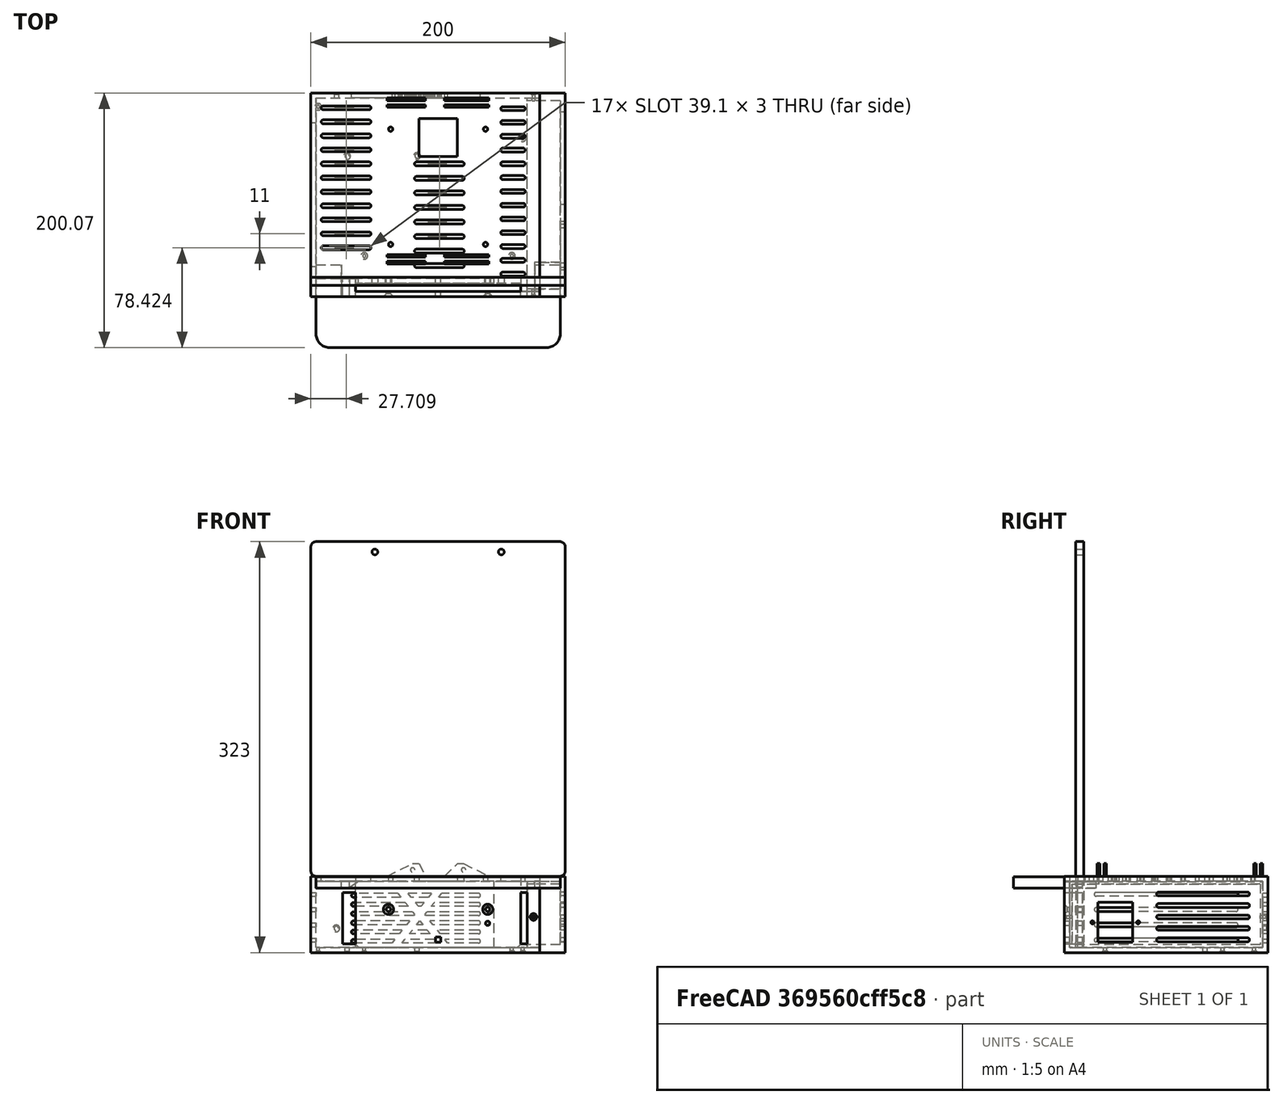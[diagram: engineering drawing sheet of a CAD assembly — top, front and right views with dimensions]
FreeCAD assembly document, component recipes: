
FREECAD ASSEMBLY — COMPONENT RECIPES ("BaseBox")

This assembly document has 5 components, labeled P0..P4 below (a component is one placed body or linked part). 2 of them carry a construction recipe — the FreeCAD feature program that regenerates the part from scratch, quoted from this document or its linked companion documents; the rest are supplied as boundary geometry only. No exploded tour is included for this assembly.
COMPONENT P0 — recipe-attached ("Shank Shield Body", modeled in this document).
Construction recipe (the document's own serialized feature program — sketch geometry with constraints, then the solid features built on it; lengths are millimeters unless a unit is written):

FEATURE [Sketcher::SketchObject] Sketch033  label="Shank Shield Sketch"
  ArcFitTolerance = 1e-06
  AttachmentSupport = -> [XZ_Plane005]
  FullyConstrained = true
  MakeInternals = false
  MapMode = 5
  Placement = pos=(0,0,0) rot=(1,0,0;1.5708rad)
  expr: Constraints[12] = <<Monitor Chassis Parameters>>.GSBasePowerBoxHeight - <<Monitor Chassis Parameters>>.GSBasePowerBoxSideThickness
  expr: Constraints[13] = 0.5 * (<<Monitor Chassis Parameters>>.GSBasePowerBoxWidth - <<Monitor Chassis Parameters>>.GSShankShieldWidth) + 0.5 * <<Monitor Chassis Parameters>>.GSBaseBoxCapOuterWidth
  expr: Constraints[14] = <<Monitor Chassis Parameters>>.GSShankShieldWidth
  expr: Constraints[15] = 0.5 * (<<Monitor Chassis Parameters>>.GSBasePowerBoxWidth - <<Monitor Chassis Parameters>>.GSShankShieldWidth) + 0.5 * <<Monitor Chassis Parameters>>.GSBaseBoxCapOuterWidth
  expr: Constraints[16] = <<Monitor Chassis Parameters>>.GSTowerFourthFloorHeight + 2 * <<Monitor Chassis Parameters>>.GSTowerFloorThickness
  expr: Constraints[22] = <<Monitor Chassis Parameters>>.GSShankShieldCornerFilletRadius
  expr: Constraints[43] = <<Monitor Chassis Parameters>>.GSShankShieldCornerFilletRadius
  expr: Constraints[44] = <<Monitor Chassis Parameters>>.GSShankShieldCornerFilletRadius
  expr: Constraints[45] = <<Monitor Chassis Parameters>>.GSShankShieldCornerFilletRadius
  expr: Constraints[46] = <<Monitor Chassis Parameters>>.GSShankShieldCornerFilletRadius
  expr: Constraints[47] = <<Monitor Chassis Parameters>>.GSShankShieldCornerFilletRadius
  expr: Constraints[48] = <<Monitor Chassis Parameters>>.GSTowerFeetThickness + <<Monitor Chassis Parameters>>.GSTowerFourthFloorHeight - 1.5 * <<Monitor Chassis Parameters>>.GSM4TappingScrewHoleDiameter
  expr: Constraints[49] = <<Monitor Chassis Parameters>>.GSM4TappingScrewHoleDiameter + 1.1
  expr: Constraints[50] = <<Monitor Chassis Parameters>>.GSM4TappingScrewHoleDiameter + 1.1
  expr: Constraints[52] = <<Monitor Chassis Parameters>>.GSBackPlateWidth - 3 * <<Monitor Chassis Parameters>>.GSM4TappingScrewHoleDiameter
  expr: Constraints[53] = 0.5 * (<<Monitor Chassis Parameters>>.GSBasePowerBoxWidth + <<Monitor Chassis Parameters>>.GSBaseBoxCapOuterWidth - <<Monitor Chassis Parameters>>.GSBackPlateWidth) + 1.5 * <<Monitor Chassis Parameters>>.GSM4TappingScrewHoleDiameter
  expr: Constraints[54] = <<Monitor Chassis Parameters>>.GSM4TappingScrewHoleDiameter + 1.1
  expr: Constraints[55] = <<Monitor Chassis Parameters>>.GSM4TappingScrewHoleDiameter + 1.1
  expr: Constraints[57] = <<Monitor Chassis Parameters>>.GSShankShieldBaseBoxSecurementHoleHeight
  expr: Constraints[58] = 0.5 * (<<Monitor Chassis Parameters>>.GSBasePowerBoxWidth + <<Monitor Chassis Parameters>>.GSBaseBoxCapOuterWidth) - 0.3 * <<Monitor Chassis Parameters>>.GSShankShieldWidth
  expr: Constraints[59] = 0.5 * (<<Monitor Chassis Parameters>>.GSBasePowerBoxWidth + <<Monitor Chassis Parameters>>.GSBaseBoxCapOuterWidth) + 0.3 * <<Monitor Chassis Parameters>>.GSShankShieldWidth
  sketch-geometry (24):
    g0: LineSegment StartX=4.24264 StartY=319 StartZ=0 EndX=195.757 EndY=319 EndZ=0
    g1: LineSegment StartX=200 StartY=314.757 StartZ=0 EndX=200 EndY=60.2426 EndZ=0
    g2: LineSegment StartX=195.757 StartY=56 StartZ=0 EndX=165 EndY=56 EndZ=0
    g3: LineSegment StartX=165 StartY=56 StartZ=0 EndX=165 EndY=4.24264 EndZ=0
    g4: LineSegment StartX=160.757 StartY=0 StartZ=0 EndX=39.2426 EndY=0 EndZ=0
    g5: LineSegment StartX=35 StartY=4.24264 StartZ=0 EndX=35 EndY=56 EndZ=0
    g6: LineSegment StartX=35 StartY=56 StartZ=0 EndX=4.24264 EndY=56 EndZ=0
    g7: LineSegment StartX=0 StartY=60.2426 StartZ=0 EndX=0 EndY=314.757 EndZ=0
    g8: ArcOfCircle CenterX=4.24264 CenterY=314.757 CenterZ=0 NormalX=0 NormalY=0 NormalZ=1 AngleXU=0 Radius=4.24264 StartAngle=1.5708 EndAngle=3.14159
    g9: GeomPoint [constr] X=0 Y=319 Z=0
    g10: ArcOfCircle CenterX=195.757 CenterY=314.757 CenterZ=0 NormalX=0 NormalY=0 NormalZ=1 AngleXU=0 Radius=4.24264 StartAngle=2.7e-15 EndAngle=1.5708
    g11: GeomPoint [constr] X=200 Y=319 Z=0
    g12: ArcOfCircle CenterX=4.24264 CenterY=60.2426 CenterZ=0 NormalX=0 NormalY=0 NormalZ=1 AngleXU=0 Radius=4.24264 StartAngle=3.14159 EndAngle=4.71239
    g13: GeomPoint [constr] X=0 Y=56 Z=0
    g14: ArcOfCircle CenterX=195.757 CenterY=60.2426 CenterZ=0 NormalX=0 NormalY=0 NormalZ=1 AngleXU=0 Radius=4.24264 StartAngle=4.71239 EndAngle=6.28319
    g15: GeomPoint [constr] X=200 Y=56 Z=0
    g16: ArcOfCircle CenterX=39.2426 CenterY=4.24264 CenterZ=0 NormalX=0 NormalY=0 NormalZ=1 AngleXU=0 Radius=4.24264 StartAngle=3.14159 EndAngle=4.71239
    g17: GeomPoint [constr] X=35 Y=0 Z=0
    g18: ArcOfCircle CenterX=160.757 CenterY=4.24264 CenterZ=0 NormalX=0 NormalY=0 NormalZ=1 AngleXU=0 Radius=4.24264 StartAngle=4.71239 EndAngle=6.28319
    g19: GeomPoint [constr] X=165 Y=0 Z=0
    g20: Circle CenterX=50.3 CenterY=310.9 CenterZ=0 NormalX=0 NormalY=0 NormalZ=1 AngleXU=0 Radius=2.25
    g21: Circle CenterX=149.7 CenterY=310.9 CenterZ=0 NormalX=0 NormalY=0 NormalZ=1 AngleXU=0 Radius=2.25
    g22: Circle CenterX=61 CenterY=30 CenterZ=0 NormalX=0 NormalY=0 NormalZ=1 AngleXU=0 Radius=2.25
    g23: Circle CenterX=139 CenterY=30 CenterZ=0 NormalX=0 NormalY=0 NormalZ=1 AngleXU=0 Radius=2.25
  constraints (60):
    c: Horizontal(g0)
    c: Vertical(g1)
    c: Horizontal(g2)
    c: Coincident(g3,g2)
    c: PointOnObject(g19,g-1)
    c: Vertical(g3)
    c: Horizontal(g4)
    c: Vertical(g5)
    c: Coincident(g6,g5)
    c: Horizontal(g6)
    c: Vertical(g7)
    c: Horizontal(g5,g2)
    c: DistanceY(g17,g5) = 56
    c: DistanceX(g13,g5) = 35
    c: DistanceX(g5,g2) = 130
    c: DistanceX(g2,g15) = 35
    c: DistanceY(g13,g9) = 263
    c: PointOnObject(g9,g0)
    c: PointOnObject(g9,g7)
    c: Tangent(g0,g8) = 1.5708
    c: Tangent(g7,g8) = 1.5708
    c: Vertical(g13,g-1)
    c: Distance(g9,g8) = 6
    c: PointOnObject(g11,g0)
    c: PointOnObject(g11,g1)
    c: Tangent(g0,g10) = 1.5708
    c: Tangent(g1,g10) = 1.5708
    c: PointOnObject(g13,g6)
    c: PointOnObject(g13,g7)
    c: Tangent(g6,g12) = 1.5708
    c: Tangent(g7,g12) = 1.5708
    c: PointOnObject(g15,g1)
    c: PointOnObject(g15,g2)
    c: Tangent(g1,g14) = 1.5708
    c: Tangent(g2,g14) = 1.5708
    c: PointOnObject(g17,g4)
    c: PointOnObject(g17,g5)
    c: Tangent(g4,g16) = 1.5708
    c: Tangent(g5,g16) = 1.5708
    c: PointOnObject(g19,g3)
    c: PointOnObject(g19,g4)
    c: Tangent(g3,g18) = 1.5708
    c: Tangent(g4,g18) = 1.5708
    c: Distance(g11,g10) = 6
    c: Distance(g13,g12) = 6
    c: Distance(g14,g15) = 6
    c: Distance(g19,g18) = 6
    c: Distance(g16,g17) = 6
    c: DistanceY(g5,g20) = 254.9
    c: Diameter(g20) = 4.5
    c: Diameter(g21) = 4.5
    c: Horizontal(g20,g21)
    c: DistanceX(g20,g21) = 99.4
    c: DistanceX(g-1,g20) = 50.3
    c: Diameter(g22) = 4.5
    c: Diameter(g23) = 4.5
    c: Horizontal(g22,g23)
    c: DistanceY(g-1,g22) = 30
    c: DistanceX(g-1,g22) = 61
    c: DistanceX(g-1,g23) = 139
FEATURE [PartDesign::Pad] Pad009  label="Shank Shield Pad"
  Direction = (0,-1,2e-16)
  Length = 6.35
  Length2 = 10
  Placement = pos=(0,0,0) rot=(1,0,0;1.5708rad)
  Profile = -> Sketch033
  ReferenceAxis = -> Sketch033 [N_Axis]
  Suppressed = false
  Type = 0
  expr: Length = <<Monitor Chassis Parameters>>.GSShankShieldThickness
FEATURE [PartDesign::Body] Body004  label="Shank Shield Body"
  AllowCompound = false
  Group = -> [Sketch033,Pad009]
  Origin = -> Origin005
  Placement = pos=(0,-64.8,0) rot=(0,0,1;0rad)
  Tip = -> Pad009
COMPONENT P1 — geometry summary ("JR-101-1F008"; no construction recipe available for this part):
  bounding box: 44.0 x 33.0 x 27.7 mm
  tessellated surface: 14,122 triangles
  volume: 8508 mm^3 (21% of its bounding box)
COMPONENT P2 — geometry summary ("LRS-154"; no construction recipe available for this part):
  bounding box: 159.0 x 97.0 x 30.0 mm
  tessellated surface: 83,726 triangles
  volume: 73054 mm^3 (16% of its bounding box)
COMPONENT P3 — recipe-attached ("Tower Part", modeled in this document).
Construction recipe (the document's own serialized feature program — sketch geometry with constraints, then the solid features built on it; lengths are millimeters unless a unit is written):

FEATURE [Sketcher::SketchObject] Sketch  label="BaseBox Left Side Sketch"
  ArcFitTolerance = 1e-06
  AttachmentSupport = -> [YZ_Plane001]
  FullyConstrained = true
  MakeInternals = false
  MapMode = 5
  Placement = pos=(0,0,0) rot=(0.57735,0.57735,0.57735;2.0944rad)
  expr: Constraints[10] = <<Monitor Chassis Parameters>>.GSBasePowerBoxHeight - 2 * <<Monitor Chassis Parameters>>.GSBasePowerBoxSideThickness
  expr: Constraints[8] = <<Monitor Chassis Parameters>>.GSBasePowerBoxDepth - 2 * <<Monitor Chassis Parameters>>.GSBasePowerBoxSideThickness
  expr: Constraints[9] = 0.5 * (<<Monitor Chassis Parameters>>.GSBasePowerBoxDepth - 2 * <<Monitor Chassis Parameters>>.GSBasePowerBoxSideThickness)
  sketch-geometry (4):
    g0: LineSegment StartX=-76 StartY=52 StartZ=0 EndX=-76 EndY=0 EndZ=0
    g1: LineSegment StartX=-76 StartY=0 StartZ=0 EndX=76 EndY=0 EndZ=0
    g2: LineSegment StartX=76 StartY=0 StartZ=0 EndX=76 EndY=52 EndZ=0
    g3: LineSegment StartX=76 StartY=52 StartZ=0 EndX=-76 EndY=52 EndZ=0
  constraints (12):
    c: Coincident(g0,g1)
    c: Coincident(g1,g2)
    c: Coincident(g2,g3)
    c: Coincident(g3,g0)
    c: Vertical(g0)
    c: Vertical(g2)
    c: Horizontal(g1)
    c: Horizontal(g3)
    c: DistanceX(g0,g1) = 152
    c: DistanceX(g0,g-1) = 76
    c: DistanceY(g0,g0) = 52
    c: Horizontal(g-1,g0)
FEATURE [PartDesign::Pad] Pad  label="BaseBox Left Side Pad"
  Direction = (1,0,0)
  Length = 4
  Length2 = 10
  Placement = pos=(0,0,0) rot=(1,1,1;2.0944rad)
  Profile = -> Sketch
  ReferenceAxis = -> Sketch [N_Axis]
  Suppressed = false
  Type = 0
  expr: Length = <<Monitor Chassis Parameters>>.GSBasePowerBoxSideThickness
FEATURE [Sketcher::SketchObject] Sketch001  label="BaseBox Enclosure Sketch"
  ArcFitTolerance = 1e-06
  AttachmentSupport = -> [YZ_Plane001]
  FullyConstrained = true
  MakeInternals = false
  MapMode = 5
  Placement = pos=(0,0,0) rot=(0.57735,0.57735,0.57735;2.0944rad)
  expr: Constraints[16] = 0.5 * (<<Monitor Chassis Parameters>>.GSBasePowerBoxDepth - 2 * <<Monitor Chassis Parameters>>.GSBasePowerBoxSideThickness)
  expr: Constraints[17] = <<Monitor Chassis Parameters>>.GSBasePowerBoxDepth - 2 * <<Monitor Chassis Parameters>>.GSBasePowerBoxSideThickness
  expr: Constraints[18] = <<Monitor Chassis Parameters>>.GSBasePowerBoxHeight - 2 * <<Monitor Chassis Parameters>>.GSBasePowerBoxSideThickness
  expr: Constraints[19] = <<Monitor Chassis Parameters>>.GSBasePowerBoxSideThickness
  expr: Constraints[20] = <<Monitor Chassis Parameters>>.GSBasePowerBoxSideThickness
  expr: Constraints[21] = <<Monitor Chassis Parameters>>.GSBasePowerBoxSideThickness
  expr: Constraints[23] = <<Monitor Chassis Parameters>>.GSBasePowerBoxSideThickness
  sketch-geometry (8):
    g0: LineSegment StartX=-80 StartY=56 StartZ=0 EndX=-80 EndY=-4 EndZ=0
    g1: LineSegment StartX=-80 StartY=-4 StartZ=0 EndX=80 EndY=-4 EndZ=0
    g2: LineSegment StartX=80 StartY=-4 StartZ=0 EndX=80 EndY=56 EndZ=0
    g3: LineSegment StartX=80 StartY=56 StartZ=0 EndX=-80 EndY=56 EndZ=0
    g4: LineSegment StartX=-76 StartY=52 StartZ=0 EndX=-76 EndY=0 EndZ=0
    g5: LineSegment StartX=-76 StartY=0 StartZ=0 EndX=76 EndY=0 EndZ=0
    g6: LineSegment StartX=76 StartY=0 StartZ=0 EndX=76 EndY=52 EndZ=0
    g7: LineSegment StartX=76 StartY=52 StartZ=0 EndX=-76 EndY=52 EndZ=0
  constraints (24):
    c: Coincident(g0,g1)
    c: Coincident(g1,g2)
    c: Coincident(g2,g3)
    c: Coincident(g3,g0)
    c: Vertical(g0)
    c: Vertical(g2)
    c: Horizontal(g1)
    c: Horizontal(g3)
    c: Coincident(g4,g5)
    c: Coincident(g5,g6)
    c: Coincident(g6,g7)
    c: Coincident(g7,g4)
    c: Vertical(g4)
    c: Vertical(g6)
    c: Horizontal(g5)
    c: Horizontal(g7)
    c: DistanceX(g4,g-1) = 76
    c: DistanceX(g4,g5) = 152
    c: DistanceY(g4,g4) = 52
    c: DistanceX(g0,g4) = 4
    c: DistanceY(g4,g0) = 4
    c: DistanceX(g5,g1) = 4
    c: Horizontal(g4,g-1)
    c: DistanceY(g0,g4) = 4
FEATURE [PartDesign::Pad] Pad001  label="BaseBox Enclosure Pad"
  BaseFeature = -> Pad
  Direction = (1,0,0)
  Length = 180
  Length2 = 10
  Placement = pos=(0,0,0) rot=(1,1,1;2.0944rad)
  Profile = -> Sketch001
  ReferenceAxis = -> Sketch001 [N_Axis]
  Suppressed = false
  Type = 0
  expr: Length = <<Monitor Chassis Parameters>>.GSBasePowerBoxWidth
FEATURE [PartDesign::Plane] DatumPlane  label="BaseBox Side Datum Plane"
  AttachmentOffset = pos=(0,0,-80) rot=(0,0,1;0rad)
  AttachmentSupport = -> [XZ_Plane001]
  Length = 249.363
  MapMode = 5
  Placement = pos=(0,80,-1.78e-14) rot=(1,0,0;1.5708rad)
  ResizeMode = 0
  Width = 119.363
  expr: .AttachmentOffset.Base.z = -0.5 * <<Monitor Chassis Parameters>>.GSBasePowerBoxDepth
FEATURE [Sketcher::SketchObject] Sketch002  label="BaseBox Side Screw Holes Sketch"
  ArcFitTolerance = 1e-06
  AttachmentSupport = -> [DatumPlane]
  FullyConstrained = true
  MakeInternals = false
  MapMode = 5
  Placement = pos=(0,80,-1.78e-14) rot=(1,0,0;1.5708rad)
  expr: Constraints[0] = <<Monitor Chassis Parameters>>.GSBasePowerBoxSupplyMountingScrewSize
  expr: Constraints[1] = <<Monitor Chassis Parameters>>.GSBasePowerBoxSupplyMountingScrewSize
  expr: Constraints[2] = <<Monitor Chassis Parameters>>.GSBasePowerBoxSupplyMountingLeftScrewOffsetFromRight
  expr: Constraints[3] = <<Monitor Chassis Parameters>>.GSBasePowerBoxSupplyMountingScrewOffsetFromRight
  expr: Constraints[4] = <<Monitor Chassis Parameters>>.GSBasePowerBoxSupplyMountingRightScrewHeight1
  expr: Constraints[5] = <<Monitor Chassis Parameters>>.GSBasePowerBoxSupplyMountingLeftScrewHeight
  sketch-geometry (2):
    g0: Circle CenterX=94 CenterY=15 CenterZ=0 NormalX=0 NormalY=0 NormalZ=1 AngleXU=0 Radius=1.7
    g1: Circle CenterX=20 CenterY=15 CenterZ=0 NormalX=0 NormalY=0 NormalZ=1 AngleXU=0 Radius=1.7
  constraints (6):
    c: Diameter(g0) = 3.4
    c: Diameter(g1) = 3.4
    c: DistanceX(g-1,g0) = 94
    c: DistanceX(g-1,g1) = 20
    c: DistanceY(g-1,g1) = 15
    c: DistanceY(g-1,g0) = 15
FEATURE [PartDesign::Hole] Hole  label="BaseBox Side Screw Holes"
  BaseFeature = -> Pad001
  CustomThreadClearance = 0
  Depth = 25
  DepthType = 0
  Diameter = 3.4
  DrillForDepth = false
  DrillPoint = 1
  DrillPointAngle = 118
  HoleCutCountersinkAngle = 90
  HoleCutCustomValues = false
  HoleCutDepth = 0
  HoleCutDiameter = 5.3
  HoleCutType = 2
  ModelThread = false
  Placement = pos=(0,0,0) rot=(1,1,1;2.0944rad)
  Profile = -> Sketch002
  Reversed = true
  Suppressed = false
  Tapered = false
  TaperedAngle = 90
  ThreadClass = 0
  ThreadDepth = 25
  ThreadDepthType = 0
  ThreadDirection = 0
  ThreadFit = 0
  ThreadSize = 0
  ThreadType = 0
  Threaded = false
  UseCustomThreadClearance = false
  expr: Diameter = <<Monitor Chassis Parameters>>.GSBasePowerBoxSupplyMountingScrewSize
  expr: HoleCutDiameter = <<Monitor Chassis Parameters>>.GSM3BoltCountersinkDiameter
FEATURE [PartDesign::Plane] DatumPlane001  label="BaseBox Bottom Datum Plane"
  AttachmentOffset = pos=(0,0,-4) rot=(0,0,1;0rad)
  AttachmentSupport = -> [XY_Plane001]
  Length = 258.609
  MapMode = 5
  Placement = pos=(0,0,-4) rot=(0,0,1;0rad)
  ResizeMode = 0
  Width = 197.609
  expr: .AttachmentOffset.Base.z = -<<Monitor Chassis Parameters>>.GSBasePowerBoxSideThickness
FEATURE [Sketcher::SketchObject] Sketch003  label="BaseBox Bottom Screw Holes Sketch"
  ArcFitTolerance = 1e-06
  AttachmentSupport = -> [DatumPlane001]
  FullyConstrained = true
  MakeInternals = false
  MapMode = 5
  Placement = pos=(0,0,-4) rot=(0,0,1;0rad)
  expr: Constraints[1] = <<Monitor Chassis Parameters>>.GSBasePowerBoxSupplyMountingScrewSize
  expr: Constraints[2] = <<Monitor Chassis Parameters>>.GSBasePowerBoxSupplyMountingScrewSize
  expr: Constraints[3] = <<Monitor Chassis Parameters>>.GSBasePowerBoxSupplyMountingBottomScrewsBackOffset
  expr: Constraints[4] = <<Monitor Chassis Parameters>>.GSBasePowerBoxSupplyMountingBottomScrewOffsetFromLeft1
  expr: Constraints[5] = <<Monitor Chassis Parameters>>.GSBasePowerBoxSupplyMountingBottomScrewOffsetFromLeft2
  sketch-geometry (2):
    g0: Circle CenterX=83.5 CenterY=30.5 CenterZ=0 NormalX=0 NormalY=0 NormalZ=1 AngleXU=0 Radius=1.7
    g1: Circle CenterX=28.5 CenterY=30.5 CenterZ=0 NormalX=0 NormalY=0 NormalZ=1 AngleXU=0 Radius=1.7
  constraints (6):
    c: Horizontal(g0,g1)
    c: Diameter(g0) = 3.4
    c: Diameter(g1) = 3.4
    c: DistanceY(g1) = 30.5
    c: DistanceX(g-1,g0) = 83.5
    c: DistanceX(g-1,g1) = 28.5
FEATURE [PartDesign::Hole] Hole001  label="BaseBox Bottom Screw Holes"
  BaseFeature = -> Hole
  CustomThreadClearance = 0
  Depth = 25
  DepthType = 0
  Diameter = 3.4
  DrillForDepth = false
  DrillPoint = 1
  DrillPointAngle = 118
  HoleCutCountersinkAngle = 90
  HoleCutCustomValues = false
  HoleCutDepth = 0
  HoleCutDiameter = 5.3
  HoleCutType = 2
  ModelThread = false
  Placement = pos=(0,0,0) rot=(1,1,1;2.0944rad)
  Profile = -> Sketch003
  Reversed = true
  Suppressed = false
  Tapered = false
  TaperedAngle = 90
  ThreadClass = 0
  ThreadDepth = 25
  ThreadDepthType = 0
  ThreadDirection = 0
  ThreadFit = 0
  ThreadSize = 0
  ThreadType = 0
  Threaded = false
  UseCustomThreadClearance = false
  expr: Diameter = <<Monitor Chassis Parameters>>.GSBasePowerBoxSupplyMountingScrewSize
  expr: HoleCutDiameter = <<Monitor Chassis Parameters>>.GSM3BoltCountersinkDiameter
FEATURE [Sketcher::SketchObject] Sketch005  label="BaseBox Left Side Slots Sketch"
  ArcFitTolerance = 1e-06
  AttachmentSupport = -> [YZ_Plane001]
  FullyConstrained = false
  MakeInternals = false
  MapMode = 5
  Placement = pos=(0,0,0) rot=(0.57735,0.57735,0.57735;2.0944rad)
  expr: Constraints[3] = <<Monitor Chassis Parameters>>.GSBasePowerBoxCoolingSlotWidth
  sketch-geometry (4):
    g0: LineSegment StartX=55 StartY=4.30289 StartZ=0 EndX=-55 EndY=4.30289 EndZ=0
    g1: LineSegment StartX=55 StartY=7.30289 StartZ=0 EndX=-55 EndY=7.30289 EndZ=0
    g2: ArcOfCircle CenterX=55 CenterY=5.80289 CenterZ=0 NormalX=0 NormalY=0 NormalZ=1 AngleXU=0 Radius=1.5 StartAngle=4.71239 EndAngle=7.85398
    g3: ArcOfCircle CenterX=-55 CenterY=5.80289 CenterZ=0 NormalX=0 NormalY=0 NormalZ=1 AngleXU=0 Radius=1.5 StartAngle=1.5708 EndAngle=4.71239
  constraints (13):
    c: Horizontal(g0)
    c: Horizontal(g1)
    c: Vertical(g0,g1)
    c: DistanceY(g0,g1) = 3
    c: DistanceX(g-1,g0) = 55
    c: DistanceX(g0,g-1) = 55
    c: Coincident(g2,g1)
    c: Coincident(g2,g0)
    c: Vertical(g2,g1)
    c: Vertical(g0,g1)
    c: Coincident(g3,g1)
    c: Coincident(g3,g0)
    c: Vertical(g0,g3)
FEATURE [PartDesign::Pocket] Pocket  label="BaseBox Left Side Slots Pocket"
  BaseFeature = -> Hole001
  Direction = (-1,0,0)
  Length = 0
  Length2 = 5
  Placement = pos=(0,0,0) rot=(1,1,1;2.0944rad)
  Profile = -> Sketch005
  ReferenceAxis = -> Sketch005 [N_Axis]
  Reversed = true
  Suppressed = false
  Type = 2
FEATURE [PartDesign::LinearPattern] LinearPattern
  BaseFeature = -> Pocket
  Direction = -> Z_Axis001
  Length = 36
  Mode = 1
  Occurrences = 4
  Offset = 12
  Originals = -> [Pocket]
  Placement = pos=(0,0,0) rot=(1,1,1;2.0944rad)
  Suppressed = false
  TransformMode = 0
  expr: Offset = 0.2 * <<Monitor Chassis Parameters>>.GSBasePowerBoxHeight
FEATURE [PartDesign::Plane] DatumPlane002  label="BaseBox Top DatumPlane"
  AttachmentOffset = pos=(0,0,56) rot=(0,0,1;0rad)
  AttachmentSupport = -> [XY_Plane001]
  Length = 258.609
  MapMode = 5
  Placement = pos=(0,0,56) rot=(0,0,1;0rad)
  ResizeMode = 0
  Width = 197.609
  expr: .AttachmentOffset.Base.z = <<Monitor Chassis Parameters>>.GSBasePowerBoxHeight - <<Monitor Chassis Parameters>>.GSBasePowerBoxSideThickness
FEATURE [Sketcher::SketchObject] Sketch006  label="BaseBox Top Holes Sketch"
  ArcFitTolerance = 1e-06
  AttachmentSupport = -> [DatumPlane002]
  FullyConstrained = true
  MakeInternals = false
  MapMode = 5
  Placement = pos=(0,0,56) rot=(0,0,1;0rad)
  expr: Constraints[10] = 0.5 * (<<Monitor Chassis Parameters>>.GSBasePowerBoxWidth - <<Monitor Chassis Parameters>>.GSShankShieldWidth) + 0.5 * <<Monitor Chassis Parameters>>.GSBaseBoxCapOuterWidth
  expr: Constraints[11] = 0.5 * <<Monitor Chassis Parameters>>.GSBasePowerBoxDepth - <<Monitor Chassis Parameters>>.GSBasePowerBoxSideThickness
  expr: Constraints[8] = <<Monitor Chassis Parameters>>.GSShankShieldThickness
  expr: Constraints[9] = <<Monitor Chassis Parameters>>.GSShankShieldWidth
  sketch-geometry (4):
    g0: LineSegment StartX=35 StartY=-69.65 StartZ=0 EndX=35 EndY=-76 EndZ=0
    g1: LineSegment StartX=35 StartY=-76 StartZ=0 EndX=165 EndY=-76 EndZ=0
    g2: LineSegment StartX=165 StartY=-76 StartZ=0 EndX=165 EndY=-69.65 EndZ=0
    g3: LineSegment StartX=165 StartY=-69.65 StartZ=0 EndX=35 EndY=-69.65 EndZ=0
  constraints (12):
    c: Coincident(g0,g1)
    c: Coincident(g1,g2)
    c: Coincident(g2,g3)
    c: Coincident(g3,g0)
    c: Vertical(g0)
    c: Vertical(g2)
    c: Horizontal(g1)
    c: Horizontal(g3)
    c: DistanceY(g0,g0) = 6.35
    c: DistanceX(g0,g2) = 130
    c: DistanceX(g-1,g0) = 35
    c: DistanceY(g0,g-1) = 76
FEATURE [PartDesign::Pocket] Pocket001  label="Shank Shield Pocket"
  BaseFeature = -> LinearPattern
  Direction = (0,0,-1)
  Length = 5
  Length2 = 5
  Placement = pos=(0,0,0) rot=(1,1,1;2.0944rad)
  Profile = -> Sketch006
  ReferenceAxis = -> Sketch006 [N_Axis]
  Suppressed = false
  Type = 2
FEATURE [Sketcher::SketchObject] Sketch007  label="Shank Shield Position Ribs Sketch"
  ArcFitTolerance = 1e-06
  AttachmentSupport = -> [XY_Plane001]
  FullyConstrained = true
  MakeInternals = false
  MapMode = 5
  expr: Constraints[12] = <<Monitor Chassis Parameters>>.GSBasePowerBoxSideThickness
  expr: Constraints[13] = <<Monitor Chassis Parameters>>.GSBasePowerBoxSideThickness
  expr: Constraints[14] = <<Monitor Chassis Parameters>>.GSShankShieldThickness
  expr: Constraints[15] = 0.5 * <<Monitor Chassis Parameters>>.GSBasePowerBoxDepth - <<Monitor Chassis Parameters>>.GSBasePowerBoxSideThickness
  expr: Constraints[17] = 0.5 * (<<Monitor Chassis Parameters>>.GSBasePowerBoxWidth - <<Monitor Chassis Parameters>>.GSShankShieldWidth) + 0.5 * <<Monitor Chassis Parameters>>.GSBaseBoxCapOuterWidth - <<Monitor Chassis Parameters>>.GSBasePowerBoxSideThickness
  sketch-geometry (6):
    g0: LineSegment StartX=4 StartY=-76 StartZ=0 EndX=35 EndY=-76 EndZ=0
    g1: LineSegment StartX=35 StartY=-76 StartZ=0 EndX=35 EndY=-69.65 EndZ=0
    g2: LineSegment StartX=35 StartY=-69.65 StartZ=0 EndX=144 EndY=-69.65 EndZ=0
    g3: LineSegment StartX=144 StartY=-69.65 StartZ=0 EndX=144 EndY=-65.65 EndZ=0
    g4: LineSegment StartX=144 StartY=-65.65 StartZ=0 EndX=4 EndY=-65.65 EndZ=0
    g5: LineSegment StartX=4 StartY=-65.65 StartZ=0 EndX=4 EndY=-76 EndZ=0
  constraints (18):
    c: Horizontal(g0)
    c: Coincident(g1,g0)
    c: Vertical(g1)
    c: Coincident(g2,g1)
    c: Horizontal(g2)
    c: Coincident(g3,g2)
    c: Vertical(g3)
    c: Coincident(g4,g3)
    c: Horizontal(g4)
    c: Coincident(g5,g4)
    c: Coincident(g5,g0)
    c: Vertical(g5)
    c: DistanceX(g-1,g4) = 4
    c: DistanceY(g2,g3) = 4
    c: DistanceY(g0,g1) = 6.35
    c: DistanceY(g0,g-1) = 76
    c: DistanceX(g4,g3) = 140
    c: DistanceX(g0,g0) = 31
FEATURE [PartDesign::Pad] Pad002  label="Shank Shield Position Ribs Pad"
  BaseFeature = -> Pocket001
  Direction = (0,0,1)
  Length = 52
  Length2 = 10
  Placement = pos=(0,0,0) rot=(1,1,1;2.0944rad)
  Profile = -> Sketch007
  ReferenceAxis = -> Sketch007 [N_Axis]
  Suppressed = false
  Type = 0
  expr: Length = <<Monitor Chassis Parameters>>.GSBasePowerBoxHeight - 2 * <<Monitor Chassis Parameters>>.GSBasePowerBoxSideThickness
FEATURE [Sketcher::SketchObject] Sketch008  label="Light Shield Sketch"
  ArcFitTolerance = 1e-06
  AttachmentSupport = -> [XY_Plane002]
  FullyConstrained = false
  MakeInternals = false
  MapMode = 5
  expr: Constraints[18] = <<Monitor Chassis Parameters>>.GSLightShieldTabWidth
  expr: Constraints[19] = <<Monitor Chassis Parameters>>.GSLightShieldTabWidth
  expr: Constraints[20] = <<Monitor Chassis Parameters>>.GSLightShieldTabDepth
  expr: Constraints[22] = <<Monitor Chassis Parameters>>.GSLightShieldDepth
  expr: Constraints[28] = <<Monitor Chassis Parameters>>.GSBasePowerBoxWidth + <<Monitor Chassis Parameters>>.GSBaseBoxCapOuterWidth - <<Monitor Chassis Parameters>>.GSBasePowerBoxSideThickness
  expr: Constraints[29] = <<Monitor Chassis Parameters>>.GSBasePowerBoxSideThickness
  sketch-geometry (10):
    g0: LineSegment StartX=4 StartY=-112.141 StartZ=0 EndX=4 EndY=-57.7713 EndZ=0
    g1: LineSegment StartX=4 StartY=-57.7713 StartZ=0 EndX=24 EndY=-57.7713 EndZ=0
    g2: LineSegment StartX=24 StartY=-57.7713 StartZ=0 EndX=24 EndY=-82.7713 EndZ=0
    g3: LineSegment StartX=24 StartY=-82.7713 StartZ=0 EndX=176 EndY=-82.7713 EndZ=0
    g4: LineSegment StartX=176 StartY=-82.7713 StartZ=0 EndX=176 EndY=-57.7713 EndZ=0
    g5: LineSegment StartX=176 StartY=-57.7713 StartZ=0 EndX=196 EndY=-57.7713 EndZ=0
    g6: LineSegment StartX=196 StartY=-57.7713 StartZ=0 EndX=196 EndY=-112.141 EndZ=0
    g7: LineSegment StartX=14.6305 StartY=-122.771 StartZ=0 EndX=185.37 EndY=-122.771 EndZ=0
    g8: ArcOfCircle CenterX=14.6305 CenterY=-112.141 CenterZ=0 NormalX=0 NormalY=0 NormalZ=1 AngleXU=0 Radius=10.6305 StartAngle=3.14159 EndAngle=4.71239
    g9: ArcOfCircle CenterX=185.37 CenterY=-112.141 CenterZ=0 NormalX=0 NormalY=0 NormalZ=1 AngleXU=0 Radius=10.6305 StartAngle=4.71239 EndAngle=6.28319
  constraints (30):
    c: Vertical(g0)
    c: Coincident(g1,g0)
    c: Horizontal(g1)
    c: Coincident(g2,g1)
    c: Vertical(g2)
    c: Coincident(g3,g2)
    c: Horizontal(g3)
    c: Coincident(g4,g3)
    c: Vertical(g4)
    c: Coincident(g5,g4)
    c: Horizontal(g5)
    c: Coincident(g6,g5)
    c: Vertical(g6)
    c: Horizontal(g7)
    c: Coincident(g8,g0)
    c: Coincident(g8,g7)
    c: Coincident(g9,g7)
    c: Coincident(g9,g6)
    c: DistanceX(g0,g1) = 20
    c: DistanceX(g4,g5) = 20
    c: DistanceY(g2,g1) = 25
    c: Horizontal(g1,g4)
    c: DistanceY(g7,g2) = 40
    c: Horizontal(g8,g0)
    c: Horizontal(g9,g6)
    c: Vertical(g8,g7)
    c: Vertical(g9,g7)
    c: Horizontal(g0,g6)
    c: DistanceX(g-1,g5) = 196
    c: DistanceX(g-1,g0) = 4
FEATURE [PartDesign::Pad] Pad003  label="Light Shield Pad"
  Direction = (0,0,1)
  Length = 9
  Length2 = 10
  Profile = -> Sketch008
  ReferenceAxis = -> Sketch008 [N_Axis]
  Suppressed = false
  Type = 0
  expr: Length = <<Monitor Chassis Parameters>>.GSLightShieldThickness + <<Monitor Chassis Parameters>>.GSBasePowerBoxSideThickness
FEATURE [PartDesign::Plane] DatumPlane003  label="BaseBox Front DatumPlane"
  AttachmentOffset = pos=(0,0,80) rot=(0,0,1;0rad)
  AttachmentSupport = -> [XZ_Plane001]
  Length = 249.363
  MapMode = 5
  Placement = pos=(0,-80,1.78e-14) rot=(1,0,0;1.5708rad)
  ResizeMode = 0
  Width = 119.363
  expr: .AttachmentOffset.Base.z = 0.5 * <<Monitor Chassis Parameters>>.GSBasePowerBoxDepth
FEATURE [Sketcher::SketchObject] Sketch009  label="Light Shield Tabs Sketch"
  ArcFitTolerance = 1e-06
  AttachmentSupport = -> [DatumPlane003]
  FullyConstrained = true
  MakeInternals = false
  MapMode = 5
  Placement = pos=(0,-80,1.78e-14) rot=(1,0,0;1.5708rad)
  expr: Constraints[10] = <<Monitor Chassis Parameters>>.GSBasePowerBoxSideThickness
  expr: Constraints[11] = <<Monitor Chassis Parameters>>.GSLightShieldHeight
  expr: Constraints[21] = <<Monitor Chassis Parameters>>.GSLightShieldTabThickness
  expr: Constraints[22] = <<Monitor Chassis Parameters>>.GSLightShieldTabWidth + <<Monitor Chassis Parameters>>.GSPartFitExtraToleranceDistance
  expr: Constraints[23] = <<Monitor Chassis Parameters>>.GSBasePowerBoxWidth + <<Monitor Chassis Parameters>>.GSBaseBoxCapOuterWidth - <<Monitor Chassis Parameters>>.GSBasePowerBoxSideThickness
  expr: Constraints[8] = <<Monitor Chassis Parameters>>.GSLightShieldTabWidth + 6 + <<Monitor Chassis Parameters>>.GSPartFitExtraToleranceDistance
  expr: Constraints[9] = <<Monitor Chassis Parameters>>.GSLightShieldTabThickness + 0.5 * <<Monitor Chassis Parameters>>.GSPartFitExtraToleranceDistance
  sketch-geometry (8):
    g0: LineSegment StartX=4 StartY=46.9 StartZ=0 EndX=30.2 EndY=46.9 EndZ=0
    g1: LineSegment StartX=30.2 StartY=46.9 StartZ=0 EndX=30.2 EndY=52 EndZ=0
    g2: LineSegment StartX=30.2 StartY=52 StartZ=0 EndX=4 EndY=52 EndZ=0
    g3: LineSegment StartX=4 StartY=52 StartZ=0 EndX=4 EndY=46.9 EndZ=0
    g4: LineSegment StartX=175.8 StartY=47 StartZ=0 EndX=196 EndY=47 EndZ=0
    g5: LineSegment StartX=196 StartY=47 StartZ=0 EndX=196 EndY=52 EndZ=0
    g6: LineSegment StartX=196 StartY=52 StartZ=0 EndX=175.8 EndY=52 EndZ=0
    g7: LineSegment StartX=175.8 StartY=52 StartZ=0 EndX=175.8 EndY=47 EndZ=0
  constraints (24):
    c: Coincident(g0,g1)
    c: Coincident(g1,g2)
    c: Coincident(g2,g3)
    c: Coincident(g3,g0)
    c: Horizontal(g0)
    c: Horizontal(g2)
    c: Vertical(g1)
    c: Vertical(g3)
    c: DistanceX(g2,g1) = 26.2
    c: DistanceY(g0,g2) = 5.1
    c: DistanceX(g-1,g0) = 4
    c: DistanceY(g-1,g2) = 52
    c: Coincident(g4,g5)
    c: Coincident(g5,g6)
    c: Coincident(g6,g7)
    c: Coincident(g7,g4)
    c: Horizontal(g4)
    c: Horizontal(g6)
    c: Vertical(g5)
    c: Vertical(g7)
    c: Horizontal(g6,g1)
    c: DistanceY(g4,g5) = 5
    c: DistanceX(g6,g5) = 20.2
    c: DistanceX(g-1,g5) = 196
FEATURE [PartDesign::Pocket] Pocket002  label="Light Shield Tabs Pocket"
  BaseFeature = -> Pad002
  Direction = (0,1,-2e-16)
  Length = 25
  Length2 = 5
  Placement = pos=(0,0,0) rot=(1,1,1;2.0944rad)
  Profile = -> Sketch009
  ReferenceAxis = -> Sketch009 [N_Axis]
  Suppressed = false
  Type = 0
  expr: Length = <<Monitor Chassis Parameters>>.GSLightShieldTabDepth
FEATURE [Sketcher::SketchObject] Sketch010  label="Overhang Fix Sketch 1"
  ArcFitTolerance = 1e-06
  AttachmentSupport = -> [Pad002]
  FullyConstrained = false
  MakeInternals = false
  MapMode = 5
  Placement = pos=(-1.46e-14,-65.65,7.3e-15) rot=(0.57735,0.57735,0.57735;4.18879rad)
  expr: Constraints[6] = <<Monitor Chassis Parameters>>.GSBasePowerBoxHeight - 2 * <<Monitor Chassis Parameters>>.GSBasePowerBoxSideThickness
  sketch-geometry (3):
    g0: LineSegment StartX=47 StartY=29.984 StartZ=0 EndX=52 EndY=36.9429 EndZ=0
    g1: LineSegment StartX=52 StartY=36.9429 StartZ=0 EndX=52 EndY=29.984 EndZ=0
    g2: LineSegment StartX=52 StartY=29.984 StartZ=0 EndX=47 EndY=29.984 EndZ=0
  constraints (7):
    c: Coincident(g1,g0)
    c: Vertical(g1)
    c: Coincident(g2,g1)
    c: Coincident(g2,g0)
    c: Horizontal(g2)
    c: DistanceX(g0,g1) = 5
    c: DistanceX(g-1,g1) = 52
FEATURE [PartDesign::Pocket] Pocket003  label="Overhang Fix Pocket 1"
  BaseFeature = -> Pocket002
  Direction = (0,-1,0)
  Length = 5
  Length2 = 5
  Placement = pos=(0,0,0) rot=(1,1,1;2.0944rad)
  Profile = -> Sketch010
  ReferenceAxis = -> Sketch010 [N_Axis]
  Suppressed = false
  Type = 0
FEATURE [Sketcher::SketchObject] Sketch011  label="BaseBox Cap Side Sketch"
  ArcFitTolerance = 1e-06
  AttachmentSupport = -> [YZ_Plane003]
  FullyConstrained = true
  MakeInternals = false
  MapMode = 5
  Placement = pos=(0,0,0) rot=(0.57735,0.57735,0.57735;2.0944rad)
  expr: Constraints[10] = <<Monitor Chassis Parameters>>.GSBasePowerBoxHeight
  expr: Constraints[12] = <<Monitor Chassis Parameters>>.GSM3TappingScrewHoleDiameter
  expr: Constraints[23] = <<Monitor Chassis Parameters>>.GSPowerPlugCutoutWidth
  expr: Constraints[24] = <<Monitor Chassis Parameters>>.GSPowerPlugCutoutHeight
  expr: Constraints[25] = <<Monitor Chassis Parameters>>.GSPowerPlugScrewHoleOffset
  expr: Constraints[26] = <<Monitor Chassis Parameters>>.GSPowerPlugScrewHoleOffset
  expr: Constraints[29] = 0.5 * <<Monitor Chassis Parameters>>.GSPowerPlugCutoutHeight
  expr: Constraints[8] = <<Monitor Chassis Parameters>>.GSBasePowerBoxDepth
  expr: Constraints[9] = 0.5 * <<Monitor Chassis Parameters>>.GSBasePowerBoxDepth
  sketch-geometry (10):
    g0: LineSegment StartX=-80 StartY=60 StartZ=0 EndX=-80 EndY=0 EndZ=0
    g1: LineSegment StartX=-80 StartY=0 StartZ=0 EndX=80 EndY=0 EndZ=0
    g2: LineSegment StartX=80 StartY=0 StartZ=0 EndX=80 EndY=60 EndZ=0
    g3: LineSegment StartX=80 StartY=60 StartZ=0 EndX=-80 EndY=60 EndZ=0
    g4: Circle CenterX=22 CenterY=23.75 CenterZ=0 NormalX=0 NormalY=0 NormalZ=1 AngleXU=0 Radius=1.2
    g5: Circle CenterX=58 CenterY=23.75 CenterZ=0 NormalX=0 NormalY=0 NormalZ=1 AngleXU=0 Radius=1.2
    g6: LineSegment StartX=53.75 StartY=8 StartZ=0 EndX=53.75 EndY=39.5 EndZ=0
    g7: LineSegment StartX=53.75 StartY=39.5 StartZ=0 EndX=26.25 EndY=39.5 EndZ=0
    g8: LineSegment StartX=26.25 StartY=39.5 StartZ=0 EndX=26.25 EndY=8 EndZ=0
    g9: LineSegment StartX=26.25 StartY=8 StartZ=0 EndX=53.75 EndY=8 EndZ=0
  constraints (30):
    c: Coincident(g0,g1)
    c: Coincident(g1,g2)
    c: Coincident(g2,g3)
    c: Coincident(g3,g0)
    c: Vertical(g0)
    c: Vertical(g2)
    c: Horizontal(g1)
    c: Horizontal(g3)
    c: DistanceX(g0,g1) = 160
    c: DistanceX(g0,g-1) = 80
    c: DistanceY(g0,g0) = 60
    c: Horizontal(g0,g-1)
    c: Diameter(g4) = 2.4
    c: Diameter(g5) = 2.4
    c: Horizontal(g4,g5)
    c: Coincident(g6,g7)
    c: Coincident(g7,g8)
    c: Coincident(g8,g9)
    c: Coincident(g9,g6)
    c: Vertical(g6)
    c: Vertical(g8)
    c: Horizontal(g7)
    c: Horizontal(g9)
    c: DistanceX(g7,g6) = 27.5
    c: DistanceY(g6,g6) = 31.5
    c: DistanceX(g4,g7) = 4.25
    c: DistanceX(g6,g5) = 4.25
    c: DistanceY(g-1,g8) = 8
    c: DistanceX(g5,g1) = 22
    c: DistanceY(g8,g4) = 15.75
FEATURE [PartDesign::Pad] Pad004  label="BaseBox Cap Side Pad"
  Direction = (1,0,0)
  Length = 4
  Length2 = 10
  Placement = pos=(0,0,0) rot=(1,1,1;2.0944rad)
  Profile = -> Sketch011
  ReferenceAxis = -> Sketch011 [N_Axis]
  Suppressed = false
  Type = 0
  expr: Length = <<Monitor Chassis Parameters>>.GSBasePowerBoxSideThickness
FEATURE [Sketcher::SketchObject] Sketch012  label="BaseBox Cap Inner Sketch"
  ArcFitTolerance = 1e-06
  AttachmentSupport = -> [YZ_Plane003]
  FullyConstrained = true
  MakeInternals = false
  MapMode = 5
  Placement = pos=(0,0,0) rot=(0.57735,0.57735,0.57735;2.0944rad)
  expr: Constraints[14] = <<Monitor Chassis Parameters>>.GSBasePowerBoxCapSideThickness
  expr: Constraints[15] = <<Monitor Chassis Parameters>>.GSBasePowerBoxCapSideThickness
  expr: Constraints[16] = <<Monitor Chassis Parameters>>.GSBasePowerBoxCapSideThickness
  expr: Constraints[17] = <<Monitor Chassis Parameters>>.GSBasePowerBoxCapSideThickness
  expr: Constraints[19] = 2 * <<Monitor Chassis Parameters>>.GSBasePowerBoxCapSideThickness + 0.5 * <<Monitor Chassis Parameters>>.GSPartFitExtraToleranceDistance
  expr: Constraints[21] = <<Monitor Chassis Parameters>>.GSBasePowerBoxDepth - 2 * <<Monitor Chassis Parameters>>.GSBasePowerBoxSideThickness - <<Monitor Chassis Parameters>>.GSPartFitExtraToleranceDistance
  expr: Constraints[22] = 0.5 * (<<Monitor Chassis Parameters>>.GSBasePowerBoxDepth - 2 * <<Monitor Chassis Parameters>>.GSBasePowerBoxSideThickness - <<Monitor Chassis Parameters>>.GSPartFitExtraToleranceDistance)
  expr: Constraints[23] = <<Monitor Chassis Parameters>>.GSBasePowerBoxHeight - 2 * <<Monitor Chassis Parameters>>.GSBasePowerBoxSideThickness - <<Monitor Chassis Parameters>>.GSPartFitExtraToleranceDistance
  sketch-geometry (8):
    g0: LineSegment StartX=-73.9 StartY=53.9 StartZ=0 EndX=-73.9 EndY=6.1 EndZ=0
    g1: LineSegment StartX=-73.9 StartY=6.1 StartZ=0 EndX=73.9 EndY=6.1 EndZ=0
    g2: LineSegment StartX=73.9 StartY=6.1 StartZ=0 EndX=73.9 EndY=53.9 EndZ=0
    g3: LineSegment StartX=73.9 StartY=53.9 StartZ=0 EndX=-73.9 EndY=53.9 EndZ=0
    g4: LineSegment StartX=-75.9 StartY=55.9 StartZ=0 EndX=-75.9 EndY=4.1 EndZ=0
    g5: LineSegment StartX=-75.9 StartY=4.1 StartZ=0 EndX=75.9 EndY=4.1 EndZ=0
    g6: LineSegment StartX=75.9 StartY=4.1 StartZ=0 EndX=75.9 EndY=55.9 EndZ=0
    g7: LineSegment StartX=75.9 StartY=55.9 StartZ=0 EndX=-75.9 EndY=55.9 EndZ=0
  constraints (24):
    c: Coincident(g0,g1)
    c: Coincident(g1,g2)
    c: Coincident(g2,g3)
    c: Coincident(g3,g0)
    c: Vertical(g0)
    c: Vertical(g2)
    c: Horizontal(g3)
    c: Coincident(g4,g5)
    c: Coincident(g5,g6)
    c: Coincident(g6,g7)
    c: Coincident(g7,g4)
    c: Vertical(g4)
    c: Vertical(g6)
    c: Horizontal(g7)
    c: DistanceX(g4,g0) = 2
    c: DistanceY(g0,g4) = 2
    c: DistanceY(g4,g0) = 2
    c: DistanceX(g1,g5) = 2
    c: Horizontal(g5)
    c: DistanceY(g-1,g4) = 4.1
    c: Horizontal(g1)
    c: DistanceX(g4,g5) = 151.8
    c: DistanceX(g4,g-1) = 75.9
    c: DistanceY(g4,g4) = 51.8
FEATURE [PartDesign::Pad] Pad005  label="BaseBox Cap Inner Pad"
  BaseFeature = -> Pad004
  Direction = (1,0,0)
  Length = 30
  Length2 = 10
  Placement = pos=(0,0,0) rot=(1,1,1;2.0944rad)
  Profile = -> Sketch012
  ReferenceAxis = -> Sketch012 [N_Axis]
  Suppressed = false
  Type = 0
  expr: Length = <<Monitor Chassis Parameters>>.GSBasePowerBoxCapInnerDepth
FEATURE [Sketcher::SketchObject] Sketch013  label="BackBox Cap Outer Sketch"
  ArcFitTolerance = 1e-06
  AttachmentSupport = -> [YZ_Plane003]
  FullyConstrained = true
  MakeInternals = false
  MapMode = 5
  Placement = pos=(0,0,0) rot=(0.57735,0.57735,0.57735;2.0944rad)
  expr: Constraints[16] = 2 * <<Monitor Chassis Parameters>>.GSBasePowerBoxCapSideThickness + 0.5 * <<Monitor Chassis Parameters>>.GSPartFitExtraToleranceDistance
  expr: Constraints[17] = 2 * <<Monitor Chassis Parameters>>.GSBasePowerBoxCapSideThickness + 0.5 * <<Monitor Chassis Parameters>>.GSPartFitExtraToleranceDistance
  expr: Constraints[18] = 2 * <<Monitor Chassis Parameters>>.GSBasePowerBoxCapSideThickness + 0.5 * <<Monitor Chassis Parameters>>.GSPartFitExtraToleranceDistance
  expr: Constraints[19] = 2 * <<Monitor Chassis Parameters>>.GSBasePowerBoxCapSideThickness + 0.5 * <<Monitor Chassis Parameters>>.GSPartFitExtraToleranceDistance
  expr: Constraints[20] = <<Monitor Chassis Parameters>>.GSBasePowerBoxHeight
  expr: Constraints[21] = 0.5 * <<Monitor Chassis Parameters>>.GSBasePowerBoxDepth
  expr: Constraints[22] = <<Monitor Chassis Parameters>>.GSBasePowerBoxDepth
  sketch-geometry (8):
    g0: LineSegment StartX=-75.9 StartY=55.9 StartZ=0 EndX=-75.9 EndY=4.1 EndZ=0
    g1: LineSegment StartX=-75.9 StartY=4.1 StartZ=0 EndX=75.9 EndY=4.1 EndZ=0
    g2: LineSegment StartX=75.9 StartY=4.1 StartZ=0 EndX=75.9 EndY=55.9 EndZ=0
    g3: LineSegment StartX=75.9 StartY=55.9 StartZ=0 EndX=-75.9 EndY=55.9 EndZ=0
    g4: LineSegment StartX=-80 StartY=60 StartZ=0 EndX=-80 EndY=0 EndZ=0
    g5: LineSegment StartX=-80 StartY=0 StartZ=0 EndX=80 EndY=0 EndZ=0
    g6: LineSegment StartX=80 StartY=0 StartZ=0 EndX=80 EndY=60 EndZ=0
    g7: LineSegment StartX=80 StartY=60 StartZ=0 EndX=-80 EndY=60 EndZ=0
  constraints (24):
    c: Coincident(g0,g1)
    c: Coincident(g1,g2)
    c: Coincident(g2,g3)
    c: Coincident(g3,g0)
    c: Vertical(g0)
    c: Vertical(g2)
    c: Horizontal(g1)
    c: Horizontal(g3)
    c: Coincident(g4,g5)
    c: Coincident(g5,g6)
    c: Coincident(g6,g7)
    c: Coincident(g7,g4)
    c: Vertical(g4)
    c: Vertical(g6)
    c: Horizontal(g5)
    c: Horizontal(g7)
    c: DistanceX(g4,g0) = 4.1
    c: DistanceY(g0,g4) = 4.1
    c: DistanceY(g4,g0) = 4.1
    c: DistanceX(g1,g5) = 4.1
    c: DistanceY(g4,g4) = 60
    c: DistanceX(g4,g-1) = 80
    c: DistanceX(g4,g5) = 160
    c: Horizontal(g4,g-1)
FEATURE [PartDesign::Pad] Pad006  label="BackBox Cap Outer Pad"
  BaseFeature = -> Pad005
  Direction = (1,0,0)
  Length = 20
  Length2 = 10
  Placement = pos=(0,0,0) rot=(1,1,1;2.0944rad)
  Profile = -> Sketch013
  ReferenceAxis = -> Sketch013 [N_Axis]
  Suppressed = false
  Type = 0
  expr: Length = <<Monitor Chassis Parameters>>.GSBaseBoxCapOuterWidth
FEATURE [PartDesign::Point] DatumPoint
  AttacherType = Attacher::AttachEnginePoint
  AttachmentOffset = pos=(0,0,100) rot=(0,0,1;0rad)
  AttachmentSupport = -> [YZ_Plane001]
  MapMode = 32
  Placement = pos=(100,0,0) rot=(0.57735,0.57735,0.57735;2.0944rad)
  expr: .AttachmentOffset.Base.z = 0.5 * (<<Monitor Chassis Parameters>>.GSBasePowerBoxWidth + <<Monitor Chassis Parameters>>.GSBaseBoxCapOuterWidth)
FEATURE [PartDesign::Plane] DatumPlane004  label="BaseBox Cap Front DatumPlane"
  AttachmentOffset = pos=(0,0,-80) rot=(0,0,1;0rad)
  AttachmentSupport = -> [XZ_Plane003]
  Length = 68.6748
  MapMode = 5
  Placement = pos=(0,80,-1.78e-14) rot=(1,0,0;1.5708rad)
  ResizeMode = 0
  Width = 98.6748
  expr: .AttachmentOffset.Base.z = -0.5 * <<Monitor Chassis Parameters>>.GSBasePowerBoxDepth
FEATURE [Sketcher::SketchObject] Sketch014  label="BaseBox Cap Light Shield Cutout Sketch"
  ArcFitTolerance = 1e-06
  AttachmentSupport = -> [DatumPlane004]
  FullyConstrained = true
  MakeInternals = false
  MapMode = 5
  Placement = pos=(0,80,-1.78e-14) rot=(1,0,0;1.5708rad)
  expr: Constraints[10] = <<Monitor Chassis Parameters>>.GSBasePowerBoxSideThickness
  expr: Constraints[11] = <<Monitor Chassis Parameters>>.GSLightShieldHeight + <<Monitor Chassis Parameters>>.GSBasePowerBoxSideThickness
  expr: Constraints[8] = <<Monitor Chassis Parameters>>.GSLightShieldTabThickness
  expr: Constraints[9] = <<Monitor Chassis Parameters>>.GSLightShieldTabWidth + <<Monitor Chassis Parameters>>.GSPartFitExtraToleranceDistance
  sketch-geometry (4):
    g0: LineSegment StartX=4 StartY=51 StartZ=0 EndX=24.2 EndY=51 EndZ=0
    g1: LineSegment StartX=24.2 StartY=51 StartZ=0 EndX=24.2 EndY=56 EndZ=0
    g2: LineSegment StartX=24.2 StartY=56 StartZ=0 EndX=4 EndY=56 EndZ=0
    g3: LineSegment StartX=4 StartY=56 StartZ=0 EndX=4 EndY=51 EndZ=0
  constraints (12):
    c: Coincident(g0,g1)
    c: Coincident(g1,g2)
    c: Coincident(g2,g3)
    c: Coincident(g3,g0)
    c: Horizontal(g0)
    c: Horizontal(g2)
    c: Vertical(g1)
    c: Vertical(g3)
    c: DistanceY(g0,g1) = 5
    c: DistanceX(g2,g1) = 20.2
    c: DistanceX(g-1,g2) = 4
    c: DistanceY(g-1,g2) = 56
FEATURE [PartDesign::Pocket] Pocket004  label="BaseBox Cap LIght Shield Cutout Pocket"
  BaseFeature = -> Pad006
  Direction = (0,1,-2e-16)
  Length = 27
  Length2 = 5
  Placement = pos=(0,0,0) rot=(1,1,1;2.0944rad)
  Profile = -> Sketch014
  ReferenceAxis = -> Sketch014 [N_Axis]
  Reversed = true
  Suppressed = false
  Type = 0
  expr: Length = <<Monitor Chassis Parameters>>.GSLightShieldTabDepth + 2
FEATURE [Sketcher::SketchObject] Sketch015  label="BaseBox Top Port Sketch"
  ArcFitTolerance = 1e-06
  AttachmentSupport = -> [DatumPlane002]
  FullyConstrained = true
  MakeInternals = false
  MapMode = 5
  Placement = pos=(0,0,56) rot=(0,0,1;0rad)
  expr: Constraints[10] = 0.5 * <<Monitor Chassis Parameters>>.GSBasePowerBoxTotalWidth - 0.5 * <<Monitor Chassis Parameters>>.GSBaseBoxRearAccessPortLength
  expr: Constraints[11] = <<Monitor Chassis Parameters>>.GSBaseBoxRearAccessOffsetFromCenterline
  expr: Constraints[8] = <<Monitor Chassis Parameters>>.GSBaseBoxRearAccessPortDepth
  expr: Constraints[9] = <<Monitor Chassis Parameters>>.GSBaseBoxRearAccessPortLength
  sketch-geometry (4):
    g0: LineSegment StartX=85 StartY=60 StartZ=0 EndX=85 EndY=30 EndZ=0
    g1: LineSegment StartX=85 StartY=30 StartZ=0 EndX=115 EndY=30 EndZ=0
    g2: LineSegment StartX=115 StartY=30 StartZ=0 EndX=115 EndY=60 EndZ=0
    g3: LineSegment StartX=115 StartY=60 StartZ=0 EndX=85 EndY=60 EndZ=0
  constraints (12):
    c: Coincident(g0,g1)
    c: Coincident(g1,g2)
    c: Coincident(g2,g3)
    c: Coincident(g3,g0)
    c: Vertical(g0)
    c: Vertical(g2)
    c: Horizontal(g1)
    c: Horizontal(g3)
    c: DistanceY(g0,g0) = 30
    c: DistanceX(g0,g1) = 30
    c: DistanceX(g-1,g0) = 85
    c: DistanceY(g-1,g0) = 30
FEATURE [PartDesign::Pocket] Pocket005  label="BaseBox Top Port Pocket"
  BaseFeature = -> Pocket003
  Direction = (0,0,-1)
  Length = 5
  Length2 = 5
  Placement = pos=(0,0,0) rot=(1,1,1;2.0944rad)
  Profile = -> Sketch015
  ReferenceAxis = -> Sketch015 [N_Axis]
  Suppressed = false
  Type = 2
FEATURE [Sketcher::SketchObject] Sketch016  label="BaseBox Top Tower Holes Sketch"
  ArcFitTolerance = 1e-06
  AttachmentSupport = -> [DatumPlane002]
  FullyConstrained = false
  MakeInternals = false
  MapMode = 5
  Placement = pos=(0,0,56) rot=(0,0,1;0rad)
  expr: Constraints[0] = <<Monitor Chassis Parameters>>.GSM4TappingScrewHoleDiameter
  expr: Constraints[1] = 0.5 * <<Monitor Chassis Parameters>>.GSBasePowerBoxTotalWidth - 0.5 * <<Monitor Chassis Parameters>>.GSBackPlateWidth + 0.5 * <<Monitor Chassis Parameters>>.GSBackPlateFootWidth
  expr: Constraints[3] = 0.5 * <<Monitor Chassis Parameters>>.GSBasePowerBoxTotalWidth + 0.5 * <<Monitor Chassis Parameters>>.GSBackPlateWidth - 0.5 * <<Monitor Chassis Parameters>>.GSBackPlateFootWidth
  expr: Constraints[5] = <<Monitor Chassis Parameters>>.GSM4TappingScrewHoleDiameter
  expr: Constraints[6] = <<Monitor Chassis Parameters>>.GSM4TappingScrewHoleDiameter
  expr: Constraints[7] = <<Monitor Chassis Parameters>>.GSBasePowerBoxTowerFootEdgeOffsetBackFromCenter - 0.2 * <<Monitor Chassis Parameters>>.GSBackPlateFootLengthBackward - 4
  expr: Constraints[8] = 0.8 * <<Monitor Chassis Parameters>>.GSBackPlateFootLengthBackward + <<Monitor Chassis Parameters>>.GSBackPlateFootScrewHoleForwardOffset + 2 * <<Monitor Chassis Parameters>>.GSBackPlateThickness
  sketch-geometry (4):
    g0: Circle CenterX=62.7 CenterY=51.6 CenterZ=0 NormalX=0 NormalY=0 NormalZ=1 AngleXU=0 Radius=1.7
    g1: Circle CenterX=62.7 CenterY=-39 CenterZ=0 NormalX=0 NormalY=0 NormalZ=1 AngleXU=0 Radius=1.7
    g2: Circle CenterX=137.3 CenterY=51.6 CenterZ=0 NormalX=0 NormalY=0 NormalZ=1 AngleXU=0 Radius=1.7
    g3: Circle CenterX=137.3 CenterY=-39 CenterZ=0 NormalX=0 NormalY=0 NormalZ=1 AngleXU=0 Radius=1.7
  constraints (11):
    c: Diameter(g0) = 3.4
    c: DistanceX(g-1,g1) = 62.7
    c: Horizontal(g0,g2)
    c: DistanceX(g-1,g3) = 137.3
    c: Horizontal(g1,g3)
    c: Diameter(g1) = 3.4
    c: Diameter(g3) = 3.4
    c: DistanceY(g-1,g0) = 51.6
    c: DistanceY(g1,g0) = 90.6
    c: Vertical(g2,g3)
    c: Vertical(g0,g1)
FEATURE [PartDesign::Hole] Hole002  label="BaseBox Top Tower Holes "
  BaseFeature = -> Pocket005
  CustomThreadClearance = 0
  Depth = 25
  DepthType = 0
  Diameter = 3.4
  DrillForDepth = false
  DrillPoint = 1
  DrillPointAngle = 118
  HoleCutCountersinkAngle = 90
  HoleCutCustomValues = false
  HoleCutDepth = 0
  HoleCutDiameter = 6.1
  HoleCutType = 0
  ModelThread = false
  Placement = pos=(0,0,0) rot=(1,1,1;2.0944rad)
  Profile = -> Sketch016
  Suppressed = false
  Tapered = false
  TaperedAngle = 90
  ThreadClass = 0
  ThreadDepth = 25
  ThreadDepthType = 0
  ThreadDirection = 0
  ThreadFit = 0
  ThreadSize = 0
  ThreadType = 0
  Threaded = false
  UseCustomThreadClearance = false
  expr: Diameter = <<Monitor Chassis Parameters>>.GSM4TappingScrewHoleDiameter
FEATURE [Sketcher::SketchObject] Sketch017  label="Basebox Top Cooling Slots Sketch 1"
  ArcFitTolerance = 1e-06
  AttachmentSupport = -> [DatumPlane002]
  FullyConstrained = false
  MakeInternals = false
  MapMode = 5
  Placement = pos=(0,0,56) rot=(0,0,1;0rad)
  expr: Constraints[4] = <<Monitor Chassis Parameters>>.GSBasePowerBoxCoolingSlotWidth
  sketch-geometry (4):
    g0: LineSegment StartX=9.65807 StartY=69.8545 StartZ=0 EndX=45.7597 EndY=69.8545 EndZ=0
    g1: LineSegment StartX=9.65807 StartY=66.8545 StartZ=0 EndX=45.7597 EndY=66.8545 EndZ=0
    g2: ArcOfCircle CenterX=9.65807 CenterY=68.3545 CenterZ=0 NormalX=0 NormalY=0 NormalZ=1 AngleXU=0 Radius=1.5 StartAngle=1.5708 EndAngle=4.71239
    g3: ArcOfCircle CenterX=45.7597 CenterY=68.3545 CenterZ=0 NormalX=0 NormalY=0 NormalZ=1 AngleXU=0 Radius=1.5 StartAngle=4.71239 EndAngle=7.85398
  constraints (11):
    c: Horizontal(g0)
    c: Horizontal(g1)
    c: Vertical(g0,g1)
    c: Vertical(g0,g1)
    c: DistanceY(g1,g0) = 3
    c: Coincident(g2,g0)
    c: Coincident(g2,g1)
    c: Coincident(g3,g0)
    c: Coincident(g3,g1)
    c: Vertical(g1,g3)
    c: Vertical(g1,g2)
FEATURE [Sketcher::SketchObject] Sketch018  label="Basebox Top Cooling Slots Sketch 2"
  ArcFitTolerance = 1e-06
  AttachmentSupport = -> [DatumPlane002]
  FullyConstrained = false
  MakeInternals = false
  MapMode = 5
  Placement = pos=(0,0,56) rot=(0,0,1;0rad)
  expr: Constraints[2] = <<Monitor Chassis Parameters>>.GSBasePowerBoxCoolingSlotWidth
  sketch-geometry (4):
    g0: LineSegment StartX=166.968 StartY=69.1863 StartZ=0 EndX=150.764 EndY=69.1863 EndZ=0
    g1: LineSegment StartX=150.764 StartY=66.1863 StartZ=0 EndX=166.968 EndY=66.1863 EndZ=0
    g2: ArcOfCircle CenterX=150.764 CenterY=67.6863 CenterZ=0 NormalX=0 NormalY=0 NormalZ=1 AngleXU=0 Radius=1.5 StartAngle=1.5708 EndAngle=4.71239
    g3: ArcOfCircle CenterX=166.968 CenterY=67.6863 CenterZ=0 NormalX=0 NormalY=0 NormalZ=1 AngleXU=0 Radius=1.5 StartAngle=4.71239 EndAngle=7.85398
  constraints (11):
    c: Horizontal(g0)
    c: Horizontal(g1)
    c: DistanceY(g1,g0) = 3
    c: Vertical(g0,g1)
    c: Vertical(g0,g1)
    c: Coincident(g2,g0)
    c: Coincident(g2,g1)
    c: Coincident(g3,g1)
    c: Coincident(g3,g0)
    c: Vertical(g2,g0)
    c: Vertical(g0,g3)
FEATURE [PartDesign::Pocket] Pocket007  label="Basebox Top Cooling Slots Pocket 2"
  BaseFeature = -> Hole002
  Direction = (0,0,-1)
  Length = 4
  Length2 = 5
  Placement = pos=(0,0,0) rot=(1,1,1;2.0944rad)
  Profile = -> Sketch018
  ReferenceAxis = -> Sketch018 [N_Axis]
  Suppressed = false
  Type = 0
  expr: Length = <<Monitor Chassis Parameters>>.GSBasePowerBoxSideThickness
FEATURE [PartDesign::LinearPattern] LinearPattern002  label="Basebox Top Cooling Slots Linear 2"
  BaseFeature = -> Pocket007
  Direction = -> Y_Axis001
  Length = 130
  Mode = 0
  Occurrences = 13
  Offset = 10.8333
  Originals = -> [Pocket007]
  Placement = pos=(0,0,0) rot=(1,1,1;2.0944rad)
  Reversed = true
  Suppressed = false
  TransformMode = 0
FEATURE [PartDesign::Pocket] Pocket008  label="Basebox Top Cooling Slots Pocket 1"
  BaseFeature = -> LinearPattern002
  Direction = (0,0,-1)
  Length = 4
  Length2 = 5
  Placement = pos=(0,0,0) rot=(1,1,1;2.0944rad)
  Profile = -> Sketch017
  ReferenceAxis = -> Sketch017 [N_Axis]
  Suppressed = false
  Type = 0
  expr: Length = <<Monitor Chassis Parameters>>.GSBasePowerBoxSideThickness
FEATURE [PartDesign::LinearPattern] LinearPattern003  label="Basebox Top Cooling Slots Linear 1"
  BaseFeature = -> Pocket008
  Direction = -> Y_Axis001
  Length = 110
  Mode = 0
  Occurrences = 11
  Offset = 11
  Originals = -> [Pocket008]
  Placement = pos=(0,0,0) rot=(1,1,1;2.0944rad)
  Reversed = true
  Suppressed = false
  TransformMode = 0
FEATURE [Sketcher::SketchObject] Sketch019  label="Basebox Top Cooling Slots Sketch 3"
  ArcFitTolerance = 1e-06
  AttachmentSupport = -> [DatumPlane002]
  FullyConstrained = false
  MakeInternals = false
  MapMode = 5
  Placement = pos=(0,0,56) rot=(0,0,1;0rad)
  sketch-geometry (4):
    g0: LineSegment StartX=82.9701 StartY=25.8301 StartZ=0 EndX=119.072 EndY=25.8301 EndZ=0
    g1: LineSegment StartX=82.9701 StartY=22.8301 StartZ=0 EndX=119.072 EndY=22.8301 EndZ=0
    g2: ArcOfCircle CenterX=82.9701 CenterY=24.3301 CenterZ=0 NormalX=0 NormalY=0 NormalZ=1 AngleXU=0 Radius=1.5 StartAngle=1.5708 EndAngle=4.71239
    g3: ArcOfCircle CenterX=119.072 CenterY=24.3301 CenterZ=0 NormalX=0 NormalY=0 NormalZ=1 AngleXU=0 Radius=1.5 StartAngle=4.71239 EndAngle=7.85398
  constraints (11):
    c: Horizontal(g0)
    c: Horizontal(g1)
    c: Vertical(g0,g1)
    c: Vertical(g0,g1)
    c: DistanceY(g1,g0) = 3
    c: Coincident(g2,g0)
    c: Coincident(g2,g1)
    c: Coincident(g3,g0)
    c: Coincident(g3,g1)
    c: Vertical(g1,g3)
    c: Vertical(g1,g2)
FEATURE [PartDesign::Pocket] Pocket009  label="Basebox Top Cooling Slots Pocket 3"
  BaseFeature = -> LinearPattern003
  Direction = (0,0,-1)
  Length = 4
  Length2 = 5
  Placement = pos=(0,0,0) rot=(1,1,1;2.0944rad)
  Profile = -> Sketch019
  ReferenceAxis = -> Sketch019 [N_Axis]
  Suppressed = false
  Type = 0
  expr: Length = <<Monitor Chassis Parameters>>.GSBasePowerBoxSideThickness
FEATURE [PartDesign::LinearPattern] LinearPattern004  label="Basebox Top Cooling Slots Pocket 3 LinearPattern"
  BaseFeature = -> Pocket009
  Direction = -> Y_Axis001
  Length = 80
  Mode = 0
  Occurrences = 8
  Offset = 11.4286
  Originals = -> [Pocket009]
  Placement = pos=(0,0,0) rot=(1,1,1;2.0944rad)
  Reversed = true
  Suppressed = false
  TransformMode = 0
FEATURE [Sketcher::SketchObject] Sketch020  label="Basebox Long Side Cooling Slots Sketch 1"
  ArcFitTolerance = 1e-06
  AttachmentSupport = -> [DatumPlane]
  FullyConstrained = false
  MakeInternals = false
  MapMode = 5
  Placement = pos=(0,80,-1.78e-14) rot=(1,0,0;1.5708rad)
  expr: Constraints[4] = <<Monitor Chassis Parameters>>.GSBasePowerBoxCoolingSlotWidth
  sketch-geometry (4):
    g0: LineSegment StartX=131.806 StartY=3.49127 StartZ=0 EndX=33.3924 EndY=3.49127 EndZ=0
    g1: LineSegment StartX=131.806 StartY=6.49127 StartZ=0 EndX=33.3924 EndY=6.49127 EndZ=0
    g2: ArcOfCircle CenterX=131.806 CenterY=4.99127 CenterZ=0 NormalX=0 NormalY=0 NormalZ=1 AngleXU=0 Radius=1.5 StartAngle=4.71239 EndAngle=7.85398
    g3: ArcOfCircle CenterX=33.3924 CenterY=4.99127 CenterZ=0 NormalX=0 NormalY=0 NormalZ=1 AngleXU=0 Radius=1.5 StartAngle=1.5708 EndAngle=4.71239
  constraints (11):
    c: Horizontal(g0)
    c: Horizontal(g1)
    c: Vertical(g1,g0)
    c: Vertical(g1,g0)
    c: DistanceY(g0,g1) = 3
    c: Coincident(g2,g1)
    c: Coincident(g2,g0)
    c: Coincident(g3,g1)
    c: Coincident(g3,g0)
    c: Vertical(g3,g1)
    c: Vertical(g2,g1)
FEATURE [PartDesign::Plane] DatumPlane005  label="Light Shield Side DatumPlane"
  AttachmentSupport = -> [Pad003]
  Length = 164.963
  MapMode = 5
  Placement = pos=(196,0,0) rot=(0.57735,0.57735,0.57735;2.0944rad)
  ResizeMode = 0
  Width = 67.1914
FEATURE [Sketcher::SketchObject] Sketch023  label="Light Shield Tab Cutout Sketch"
  ArcFitTolerance = 1e-06
  AttachmentSupport = -> [DatumPlane005]
  ExternalGeometry = -> [Pad003]
  FullyConstrained = true
  MakeInternals = false
  MapMode = 5
  Placement = pos=(196,0,0) rot=(0.57735,0.57735,0.57735;2.0944rad)
  expr: Constraints[11] = <<Monitor Chassis Parameters>>.GSLightShieldTabDepth
  expr: Constraints[8] = <<Monitor Chassis Parameters>>.GSBasePowerBoxSideThickness
  expr: Constraints[9] = <<Monitor Chassis Parameters>>.GSLightShieldTabThickness
  sketch-geometry (4):
    g0: LineSegment StartX=-82.7713 StartY=9 StartZ=0 EndX=-82.7713 EndY=5 EndZ=0
    g1: LineSegment StartX=-82.7713 StartY=5 StartZ=0 EndX=-57.7713 EndY=5 EndZ=0
    g2: LineSegment StartX=-57.7713 StartY=5 StartZ=0 EndX=-57.7713 EndY=9 EndZ=0
    g3: LineSegment StartX=-57.7713 StartY=9 StartZ=0 EndX=-82.7713 EndY=9 EndZ=0
  constraints (12):
    c: Coincident(g0,g1)
    c: Coincident(g1,g2)
    c: Coincident(g2,g3)
    c: Coincident(g3,g0)
    c: Vertical(g0)
    c: Vertical(g2)
    c: Horizontal(g1)
    c: Horizontal(g3)
    c: DistanceY(g0,g0) = 4
    c: DistanceY(g-1,g0) = 5
    c: Vertical(g0,g-3)
    c: DistanceX(g0,g1) = 25
FEATURE [PartDesign::Pocket] Pocket012  label="Light Shield Tab Cutout Pad"
  BaseFeature = -> Pad003
  Direction = (-1,0,0)
  Length = 5
  Length2 = 5
  Profile = -> Sketch023
  ReferenceAxis = -> Sketch023 [N_Axis]
  Suppressed = false
  Type = 1
FEATURE [PartDesign::Body] Body001  label="Light Shield Body"
  AllowCompound = false
  Group = -> [Sketch008,Pad003,DatumPlane005,Sketch023,Pocket012]
  Origin = -> Origin002
  Placement = pos=(0,2.7,46.7) rot=(0,0,1;0rad)
  Tip = -> Pocket012
FEATURE [Sketcher::SketchObject] Sketch027  label="Cap Securement Screw Sketch"
  ArcFitTolerance = 1e-06
  AttachmentSupport = -> [DatumPlane004]
  FullyConstrained = true
  MakeInternals = false
  MapMode = 5
  Placement = pos=(0,80,-1.78e-14) rot=(1,0,0;1.5708rad)
  expr: Constraints[0] = <<Monitor Chassis Parameters>>.GSM3TappingScrewHoleDiameter
  expr: Constraints[1] = <<Monitor Chassis Parameters>>.GSCapSecurementScrewOffsetHeight + <<Monitor Chassis Parameters>>.GSBasePowerBoxSideThickness
  expr: Constraints[2] = <<Monitor Chassis Parameters>>.GSCapSecurementScrewOffsetFromRightSide
  sketch-geometry (1):
    g0: Circle CenterX=25 CenterY=28 CenterZ=0 NormalX=0 NormalY=0 NormalZ=1 AngleXU=0 Radius=1.2
  constraints (3):
    c: Diameter(g0) = 2.4
    c: DistanceY(g-1,g0) = 28
    c: DistanceX(g-1,g0) = 25
FEATURE [PartDesign::Pocket] Pocket014  label="Cap Securement Screw Pocket"
  BaseFeature = -> Pocket004
  Direction = (0,1,-2e-16)
  Length = 5
  Length2 = 5
  Placement = pos=(0,0,0) rot=(1,1,1;2.0944rad)
  Profile = -> Sketch027
  ReferenceAxis = -> Sketch027 [N_Axis]
  Reversed = true
  Suppressed = false
  Type = 1
FEATURE [Sketcher::SketchObject] Sketch028  label="Right Side Cooling Slots Sketch"
  ArcFitTolerance = 1e-06
  AttachmentSupport = -> [YZ_Plane003]
  FullyConstrained = true
  MakeInternals = false
  MapMode = 5
  Placement = pos=(0,0,0) rot=(0.57735,0.57735,0.57735;2.0944rad)
  expr: Constraints[10] = <<Monitor Chassis Parameters>>.GSBasePowerBoxCoolingSlotWidth
  sketch-geometry (4):
    g0: LineSegment StartX=6 StartY=11.5 StartZ=0 EndX=-64 EndY=11.5 EndZ=0
    g1: LineSegment StartX=6 StartY=8.5 StartZ=0 EndX=-64 EndY=8.5 EndZ=0
    g2: ArcOfCircle CenterX=6 CenterY=10 CenterZ=0 NormalX=0 NormalY=0 NormalZ=1 AngleXU=0 Radius=1.5 StartAngle=4.71239 EndAngle=7.85398
    g3: ArcOfCircle CenterX=-64 CenterY=10 CenterZ=0 NormalX=0 NormalY=0 NormalZ=1 AngleXU=0 Radius=1.5 StartAngle=1.5708 EndAngle=4.71239
  constraints (14):
    c: Horizontal(g0)
    c: Horizontal(g1)
    c: Vertical(g0,g1)
    c: Vertical(g0,g1)
    c: Coincident(g2,g0)
    c: Coincident(g2,g1)
    c: Vertical(g0,g2)
    c: Coincident(g3,g0)
    c: Coincident(g3,g1)
    c: Vertical(g0,g3)
    c: DistanceY(g1,g0) = 3
    c: DistanceY(g-1,g1) = 8.5
    c: DistanceX(g-1,g1) = 6
    c: DistanceX(g0,g0) = 70
FEATURE [PartDesign::Pocket] Pocket015  label="Right Side Cooling Slots Pocket"
  BaseFeature = -> Pocket014
  Direction = (-1,0,0)
  Length = 5
  Length2 = 5
  Placement = pos=(0,0,0) rot=(1,1,1;2.0944rad)
  Profile = -> Sketch028
  ReferenceAxis = -> Sketch028 [N_Axis]
  Reversed = true
  Suppressed = false
  Type = 1
FEATURE [PartDesign::LinearPattern] LinearPattern007  label="Right Side Cooling Slots LinearPattern007"
  BaseFeature = -> Pocket015
  Direction = -> Sketch028 [V_Axis]
  Length = 36
  Mode = 0
  Occurrences = 5
  Offset = 9
  Originals = -> [Pocket015]
  Placement = pos=(0,0,0) rot=(1,1,1;2.0944rad)
  Suppressed = false
  TransformMode = 0
  expr: Length = 0.6 * <<Monitor Chassis Parameters>>.GSBasePowerBoxHeight
FEATURE [PartDesign::Body] Body002  label="Cap Body"
  AllowCompound = false
  Group = -> [Pad004,Sketch011,Pad005,Sketch012,Sketch013,Pad006,DatumPlane004,Sketch014,Pocket004,Sketch027,Pocket014,Sketch028,Pocket015,LinearPattern007]
  Origin = -> Origin003
  Placement = pos=(200,-2.18e-14,-4) rot=(0,0,1;3.14159rad)
  Tip = -> LinearPattern007
FEATURE [PartDesign::Body] Body  label="BaseBox Body"
  AllowCompound = false
  Group = -> [Sketch,Pad,Sketch001,Pad001,DatumPlane,Sketch002,Hole,DatumPlane001,Sketch003,Hole001,Sketch005,Pocket,LinearPattern,DatumPlane002,Sketch006,Pocket001,Sketch007,Pad002,DatumPlane003,Sketch009,Pocket002,Sketch010,Pocket003,DatumPoint,Sketch015,Pocket005,Sketch016,Hole002,Sketch017,Sketch018,Pocket007,LinearPattern002,Pocket008,LinearPattern003,Sketch019,Pocket009,LinearPattern004,Sketch020,+20 more]
  Origin = -> Origin001
  Tip = -> Pad008
COMPONENT P4 — geometry summary ("LRS-75 Mean Well"; no construction recipe available for this part):
  bounding box: 99.0 x 97.0 x 30.0 mm
  tessellated surface: 71,952 triangles
  volume: 42793 mm^3 (15% of its bounding box)
PROVENANCE & LICENSES
A FreeCAD (.FCStd) document from a public repository crawl; recipes are the document's own serialized feature recipes (and, for linked parts, companion documents' recipes).
License: gpl-2.0.
